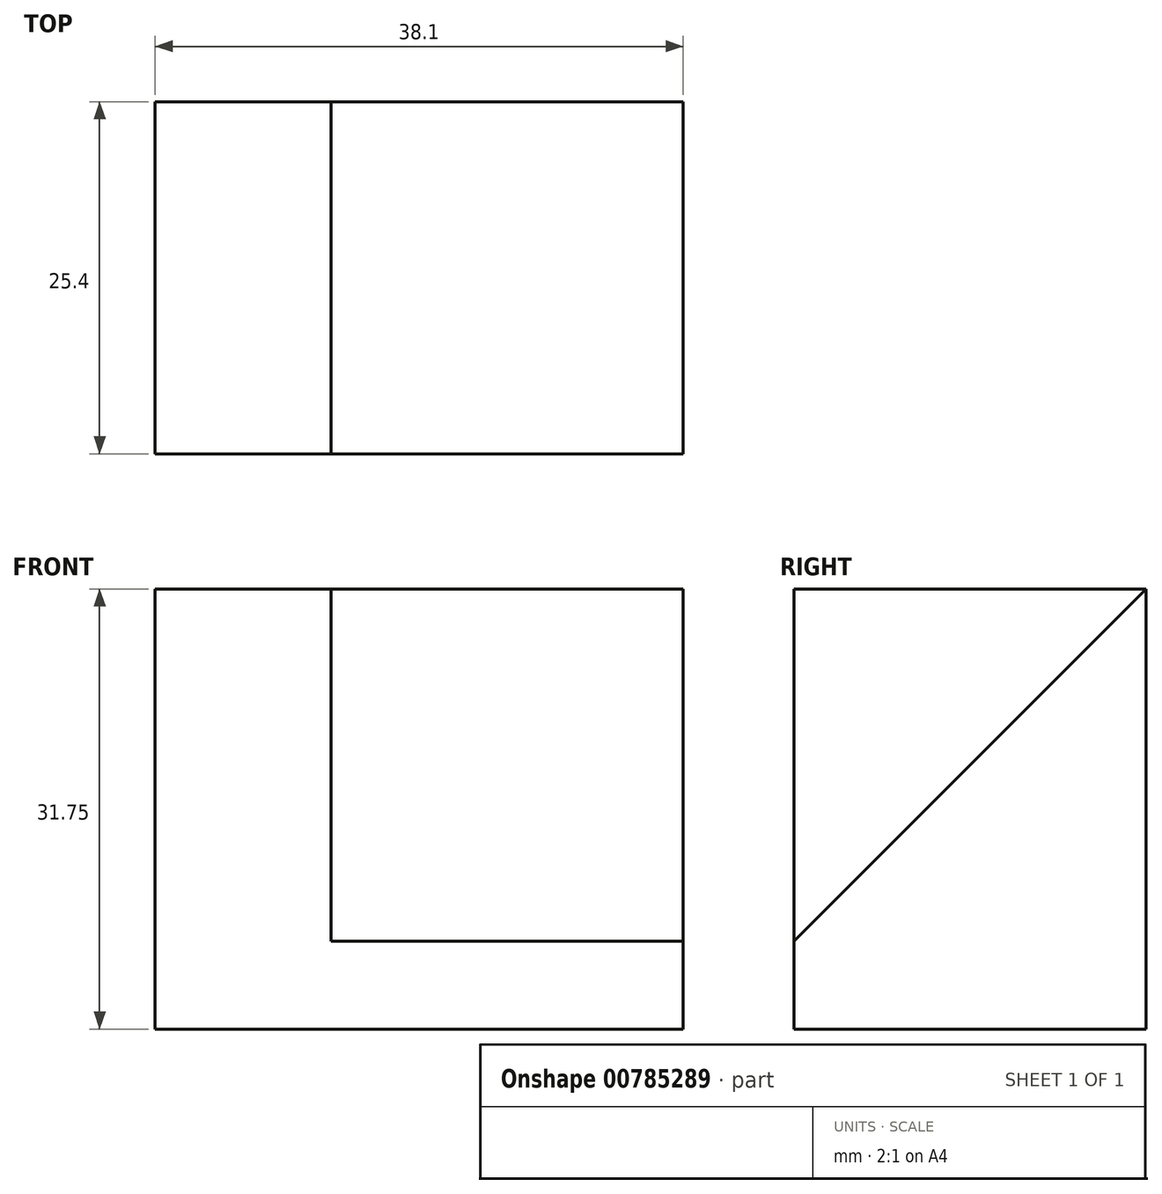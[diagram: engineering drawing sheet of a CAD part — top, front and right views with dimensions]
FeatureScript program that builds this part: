
annotation { "Feature Type Name" : "Feature", "Feature Type Description" : "" }
export const myFeature = defineFeature(function(context is Context, id is Id, definition is map)
    precondition{}
    {
        {
            var Q0;
            Q0=qCreatedBy(makeId("Front.planeOp"),FACE);
            var sketch = newSketch(context, id + "F0", { "sketchPlane" : qUnion([Q0])});
            skLineSegment(sketch, "E0", {"start": v(0, 0) * mm, "end": v(38.1, 0) * mm});
            skLineSegment(sketch, "E1", {"start": v(0, 0) * mm, "end": v(0, 31.75) * mm});
            skLineSegment(sketch, "E2", {"start": v(0, 31.75) * mm, "end": v(12.7, 31.75) * mm});
            skLineSegment(sketch, "E3", {"start": v(12.7, 31.75) * mm, "end": v(38.1, 31.75) * mm});
            skLineSegment(sketch, "E4", {"start": v(38.1, 31.75) * mm, "end": v(38.1, 0) * mm});
            skSolve(sketch);
        }
        {
            var Q0;
            Q0=makeQuery(id+"F0.imprint","IMPRINT",FACE,{"disambiguationData":[TD([[makeQuery(id+"F0.imprint","IMPRINT",EDGE,{"derivedFrom":sQuery(id+"F0.wireOp",EDGE,"E0")}),1.0]])]});
            extrude(context, id + "F1", {"entities" : qUnion([Q0]), "depth" : 25.4 * mm, "offsetDistance" : 25.4 * mm});
        }
        {
            var Q0;
            Q0=makeQuery(id+"F1.opExtrude","SWEPT_FACE",FACE,{"disambiguationData":[OSD([sQuery(id+"F0.wireOp",EDGE,"E4")])]});
            var sketch = newSketch(context, id + "F2", { "sketchPlane" : qUnion([Q0])});
            skLineSegment(sketch, "E5", {"start": v(-25.4, 0) * mm, "end": v(-25.4, 6.35) * mm});
            skLineSegment(sketch, "E6", {"start": v(-25.4, 6.35) * mm, "end": v(0, 31.75) * mm});
            skLineSegment(sketch, "E7", {"start": v(-25.4, 6.35) * mm, "end": v(-25.4, 31.75) * mm});
            skLineSegment(sketch, "E8", {"start": v(-25.4, 31.75) * mm, "end": v(0, 31.75) * mm});
            skSolve(sketch);
        }
        {
            var Q0;
            Q0=makeQuery(id+"F2.imprint","IMPRINT",FACE,{"disambiguationData":[TD([[makeQuery(id+"F2.imprint","IMPRINT",EDGE,{"derivedFrom":sQuery(id+"F2.wireOp",EDGE,"E6")}),1.0]])]});
            extrude(context, id + "F3", {"entities" : qUnion([Q0]), "operationType" : NewBodyOperationType.REMOVE, "oppositeDirection" : true, "depth" : 25.4 * mm, "offsetDistance" : 25.4 * mm});
        }
    });
